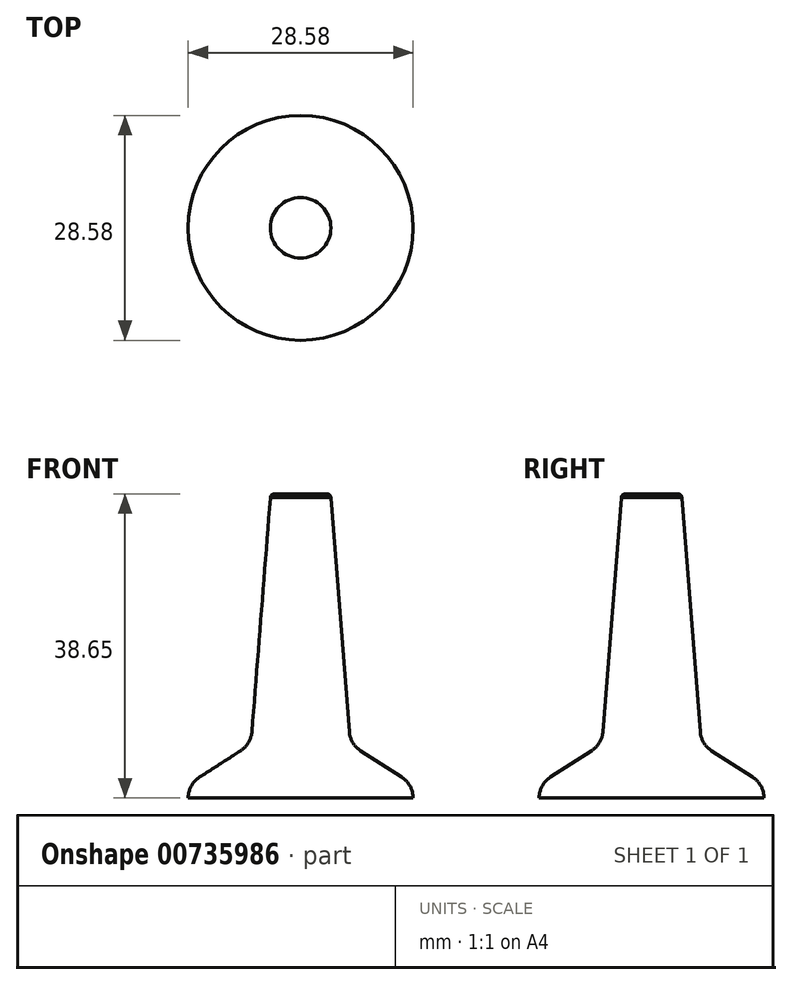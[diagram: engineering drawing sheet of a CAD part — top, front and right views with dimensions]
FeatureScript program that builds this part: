
annotation { "Feature Type Name" : "Feature", "Feature Type Description" : "" }
export const myFeature = defineFeature(function(context is Context, id is Id, definition is map)
    precondition{}
    {
        {
            var Q0;
            Q0=qCreatedBy(makeId("Front.planeOp"),FACE);
            var sketch = newSketch(context, id + "F0", { "sketchPlane" : qUnion([Q0])});
            skLineSegment(sketch, "E0.top", {"start": v(-14.29, 0) * mm, "end": v(14.29, 0) * mm});
            skLineSegment(sketch, "E0.left", {"start": v(-14.29, 25.08) * mm, "end": v(-14.29, 0) * mm});
            skPoint(sketch, "E1.visualSharp", {"position": v(14.29, 6.44) * mm});
            skPoint(sketch, "E2.visualSharp", {"position": v(14.29, 3.02) * mm});
            skLineSegment(sketch, "E3", {"start": v(0, 0) * mm, "end": v(0, 38.1) * mm});
            skLineSegment(sketch, "E4", {"start": v(3.85, 38.1) * mm, "end": v(6.18, 8.43) * mm});
            skLineSegment(sketch, "E5", {"start": v(0, 38.1) * mm, "end": v(2.61, 38.1) * mm});
            skArc(sketch, "E6", {"start": v(6.18, 8.43) * mm, "mid": v(6.62, 7.05) * mm, "end": v(7.63, 6.01) * mm});
            skArc(sketch, "E7", {"start": v(14.29, 0) * mm, "mid": v(13.9, 1.52) * mm, "end": v(12.83, 2.67) * mm});
            skLineSegment(sketch, "E8", {"start": v(7.63, 6.01) * mm, "end": v(12.83, 2.67) * mm});
            skArc(sketch, "E9", {"start": v(3.85, 38.18) * mm, "mid": v(3.85, 38.14) * mm, "end": v(3.85, 38.1) * mm});
            skLineSegment(sketch, "E10", {"start": v(3.85, 38.1) * mm, "end": v(3.85, 38.18) * mm});
            skArc(sketch, "E11.MirrorC", {"start": v(2.85, 38.28) * mm, "mid": v(3.43, 38.64) * mm, "end": v(3.85, 38.1) * mm});
            skArc(sketch, "E12.MirrorC", {"start": v(2.85, 38.28) * mm, "mid": v(2.76, 38.15) * mm, "end": v(2.61, 38.1) * mm});
            skSolve(sketch);
        }
        {
            var Q0;
            {var subQ0=sQuery(id+"F0.wireOp",EDGE,"E3");Q0=makeQuery(id+"F0.imprint","IMPRINT",FACE,{"disambiguationData":[TD([[makeQuery(id+"F0.imprint","IMPRINT",EDGE,{"derivedFrom":subQ0}),-1.0]])]});}
            var Q1;
            Q1=sQuery(id+"F0.wireOp",EDGE,"E3");
            revolve(context, id + "F1", {"surfaceOperationType" : NewSurfaceOperationType.NEW, "entities" : qUnion([Q0]), "axis" : qUnion([Q1]), "revolveType" : RevolveType.FULL});
        }
    });
